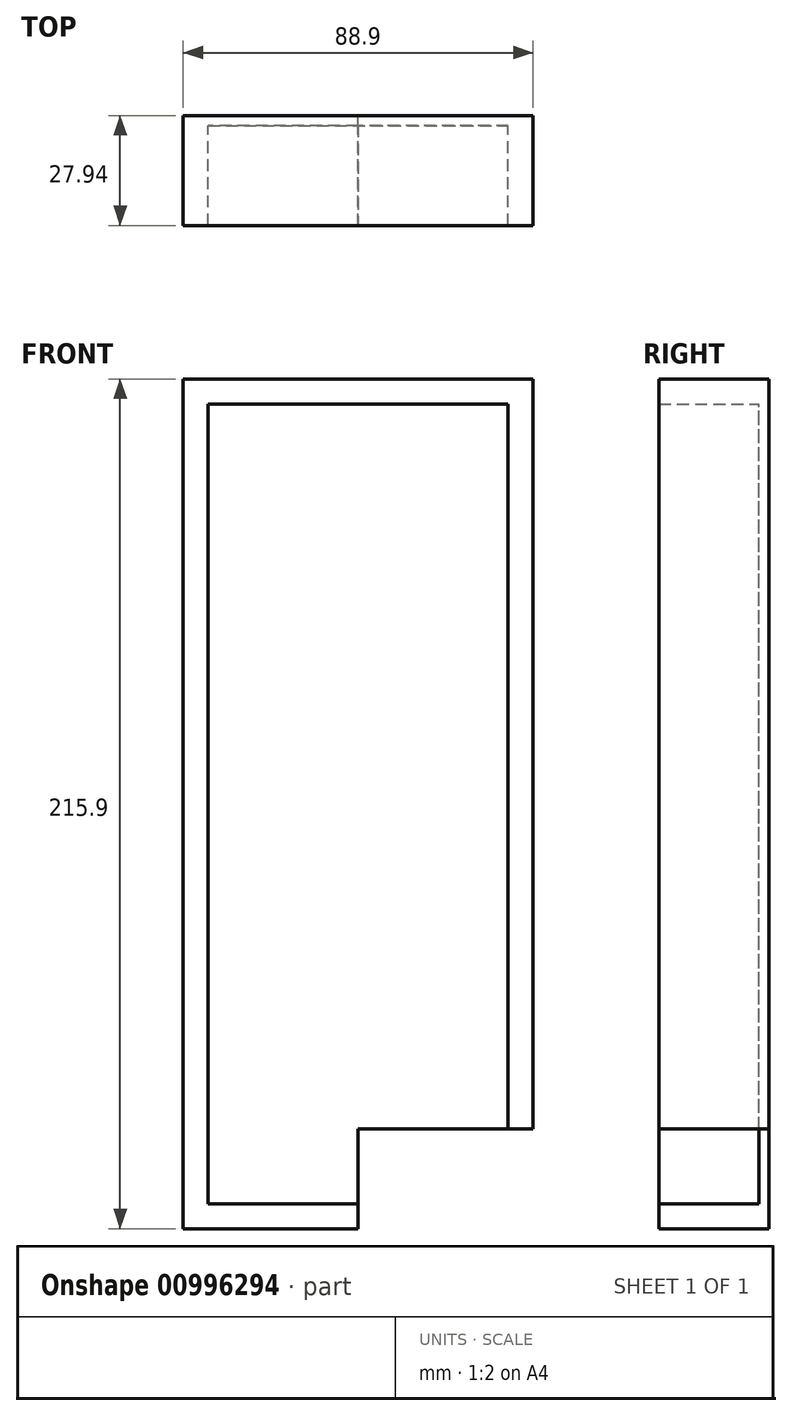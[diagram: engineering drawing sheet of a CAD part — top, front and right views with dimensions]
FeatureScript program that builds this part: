
annotation { "Feature Type Name" : "Feature", "Feature Type Description" : "" }
export const myFeature = defineFeature(function(context is Context, id is Id, definition is map)
    precondition{}
    {
        {
            var Q0;
            Q0=qCreatedBy(makeId("Front.planeOp"),FACE);
            var sketch = newSketch(context, id + "F0", { "sketchPlane" : qUnion([Q0])});
            skLineSegment(sketch, "E0.bottom", {"start": v(-90.27, 163.1) * mm, "end": v(-14.07, 163.1) * mm});
            skLineSegment(sketch, "E0.top", {"start": v(-90.27, -40.1) * mm, "end": v(-14.07, -40.1) * mm});
            skLineSegment(sketch, "E0.left", {"start": v(-90.27, 163.1) * mm, "end": v(-90.27, -40.1) * mm});
            skLineSegment(sketch, "E0.right", {"start": v(-14.07, 163.1) * mm, "end": v(-14.07, -40.1) * mm});
            skLineSegment(sketch, "E1", {"start": v(-90.27, 163.1) * mm, "end": v(-90.27, 169.45) * mm});
            skLineSegment(sketch, "E2", {"start": v(-90.27, 169.45) * mm, "end": v(-90.27, 163.1) * mm});
            skLineSegment(sketch, "E3", {"start": v(-90.27, 163.1) * mm, "end": v(-96.62, 163.1) * mm});
            skLineSegment(sketch, "E4.top", {"start": v(-90.27, 169.45) * mm, "end": v(-96.62, 169.45) * mm});
            skLineSegment(sketch, "E4.right", {"start": v(-96.62, 163.1) * mm, "end": v(-96.62, 169.45) * mm});
            skLineSegment(sketch, "E5.bottom", {"start": v(-14.07, -40.1) * mm, "end": v(-7.72, -40.1) * mm});
            skLineSegment(sketch, "E5.top", {"start": v(-14.07, -46.45) * mm, "end": v(-7.72, -46.45) * mm});
            skLineSegment(sketch, "E5.left", {"start": v(-14.07, -40.1) * mm, "end": v(-14.07, -46.45) * mm});
            skLineSegment(sketch, "E5.right", {"start": v(-7.72, -40.1) * mm, "end": v(-7.72, -46.45) * mm});
            skLineSegment(sketch, "E6.bottom", {"start": v(-7.72, -46.45) * mm, "end": v(-96.62, -46.45) * mm});
            skLineSegment(sketch, "E6.top", {"start": v(-7.72, 169.45) * mm, "end": v(-96.62, 169.45) * mm});
            skLineSegment(sketch, "E6.left", {"start": v(-7.72, -46.45) * mm, "end": v(-7.72, 169.45) * mm});
            skLineSegment(sketch, "E6.right", {"start": v(-96.62, -46.45) * mm, "end": v(-96.62, 169.45) * mm});
            skSolve(sketch);
        }
        {
            var Q0;
            Q0=makeQuery(id+"F0.imprint","IMPRINT",FACE,{"disambiguationData":[TD([[makeQuery(id+"F0.imprint","IMPRINT",EDGE,{"derivedFrom":sQuery(id+"F0.wireOp",EDGE,"E0.top")}),-1.0]])]});
            var Q1;
            {var subQ0=sQuery(id+"F0.wireOp",EDGE,"E3");Q1=makeQuery(id+"F0.imprint","IMPRINT",FACE,{"disambiguationData":[TD([[makeQuery(id+"F0.imprint","IMPRINT",EDGE,{"derivedFrom":subQ0}),-1.0]])]});}
            var Q2;
            Q2=makeQuery(id+"F0.imprint","IMPRINT",FACE,{"disambiguationData":[TD([[makeQuery(id+"F0.imprint","IMPRINT",EDGE,{"derivedFrom":sQuery(id+"F0.wireOp",EDGE,"E0.bottom")}),1.0]])]});
            var Q3;
            {var subQ0=sQuery(id+"F0.wireOp",EDGE,"E5.bottom");Q3=makeQuery(id+"F0.imprint","IMPRINT",FACE,{"disambiguationData":[TD([[makeQuery(id+"F0.imprint","IMPRINT",EDGE,{"derivedFrom":subQ0}),-1.0]])]});}
            extrude(context, id + "F1", {"entities" : qUnion([Q0, Q1, Q2, Q3]), "depth" : 27.94 * mm, "offsetDistance" : 25.4 * mm});
        }
        {
            var Q0;
            Q0=makeQuery(id+"F1.opExtrude","SWEPT_FACE",FACE,{"disambiguationData":[OSD([sQuery(id+"F0.wireOp",EDGE,"E6.bottom")])]});
            var sketch = newSketch(context, id + "F2", { "sketchPlane" : qUnion([Q0])});
            skLineSegment(sketch, "E7.bottom", {"start": v(-96.62, 0) * mm, "end": v(-7.72, 0) * mm});
            skLineSegment(sketch, "E7.top", {"start": v(-96.62, 2.54) * mm, "end": v(-7.72, 2.54) * mm});
            skLineSegment(sketch, "E7.left", {"start": v(-96.62, 0) * mm, "end": v(-96.62, 2.54) * mm});
            skLineSegment(sketch, "E7.right", {"start": v(-7.72, 0) * mm, "end": v(-7.72, 2.54) * mm});
            skSolve(sketch);
        }
        {
            var Q0;
            Q0=makeQuery(id+"F2.imprint","IMPRINT",FACE,{"disambiguationData":[TD([[makeQuery(id+"F2.imprint","IMPRINT",EDGE,{"derivedFrom":sQuery(id+"F2.wireOp",EDGE,"E7.bottom")}),-1.0]])]});
            extrude(context, id + "F3", {"entities" : qUnion([Q0]), "operationType" : NewBodyOperationType.ADD, "oppositeDirection" : true, "depth" : 209.55 * mm, "offsetDistance" : 25.4 * mm});
        }
        {
            var Q0;
            Q0=makeQuery(id+"F1.opExtrude","SWEPT_FACE",FACE,{"disambiguationData":[OSD([sQuery(id+"F0.wireOp",EDGE,"E6.bottom")])]});
            var sketch = newSketch(context, id + "F4", { "sketchPlane" : qUnion([Q0])});
            skLineSegment(sketch, "E8", {"start": v(-96.62, 13.97) * mm, "end": v(-7.72, 13.97) * mm});
            skLineSegment(sketch, "E9", {"start": v(-52.17, 27.94) * mm, "end": v(-52.17, 0) * mm});
            skCircle(sketch, "E10", {"center": v(-52.17, 13.97) * mm, "radius": 6.35 * mm});
            skSolve(sketch);
        }
        {
            var Q0;
            {var subQ0=sQuery(id+"F4.wireOp",EDGE,"E10");var subQ1=sQuery(id+"F4.wireOp",EDGE,"E8");var subQ2=makeQuery(id+"F4.imprint","INTERSECT",VERTEX,{"disambiguationData":[OD(0.0)],"derivedFrom":[subQ1,subQ0]});Q0=makeQuery(id+"F4.imprint","IMPRINT",FACE,{"disambiguationData":[TD([[makeQuery(id+"F4.imprint","IMPRINT",EDGE,{"disambiguationData":[TD([[subQ2,-1.0]])],"derivedFrom":subQ1}),1.0]])]});}
            var Q1;
            {var subQ0=sQuery(id+"F4.wireOp",EDGE,"E9");var subQ1=sQuery(id+"F4.wireOp",EDGE,"E8");var subQ2=makeQuery(id+"F4.imprint","INTERSECT",VERTEX,{"derivedFrom":[subQ1,subQ0]});Q1=makeQuery(id+"F4.imprint","IMPRINT",FACE,{"disambiguationData":[TD([[makeQuery(id+"F4.imprint","IMPRINT",EDGE,{"disambiguationData":[TD([[subQ2,-1.0]])],"derivedFrom":subQ1}),1.0]])]});}
            var Q2;
            {var subQ0=sQuery(id+"F4.wireOp",EDGE,"E9");var subQ1=sQuery(id+"F4.wireOp",EDGE,"E8");var subQ2=makeQuery(id+"F4.imprint","INTERSECT",VERTEX,{"derivedFrom":[subQ1,subQ0]});Q2=makeQuery(id+"F4.imprint","IMPRINT",FACE,{"disambiguationData":[TD([[makeQuery(id+"F4.imprint","IMPRINT",EDGE,{"disambiguationData":[TD([[subQ2,-1.0]])],"derivedFrom":subQ1}),-1.0]])]});}
            var Q3;
            {var subQ0=sQuery(id+"F4.wireOp",EDGE,"E10");var subQ1=sQuery(id+"F4.wireOp",EDGE,"E8");var subQ2=makeQuery(id+"F4.imprint","INTERSECT",VERTEX,{"disambiguationData":[OD(0.0)],"derivedFrom":[subQ1,subQ0]});Q3=makeQuery(id+"F4.imprint","IMPRINT",FACE,{"disambiguationData":[TD([[makeQuery(id+"F4.imprint","IMPRINT",EDGE,{"disambiguationData":[TD([[subQ2,-1.0]])],"derivedFrom":subQ1}),-1.0]])]});}
            extrude(context, id + "F5", {"entities" : qUnion([Q0, Q1, Q2, Q3]), "operationType" : NewBodyOperationType.REMOVE, "oppositeDirection" : true, "depth" : 25.4 * mm, "offsetDistance" : 25.4 * mm});
        }
    });
